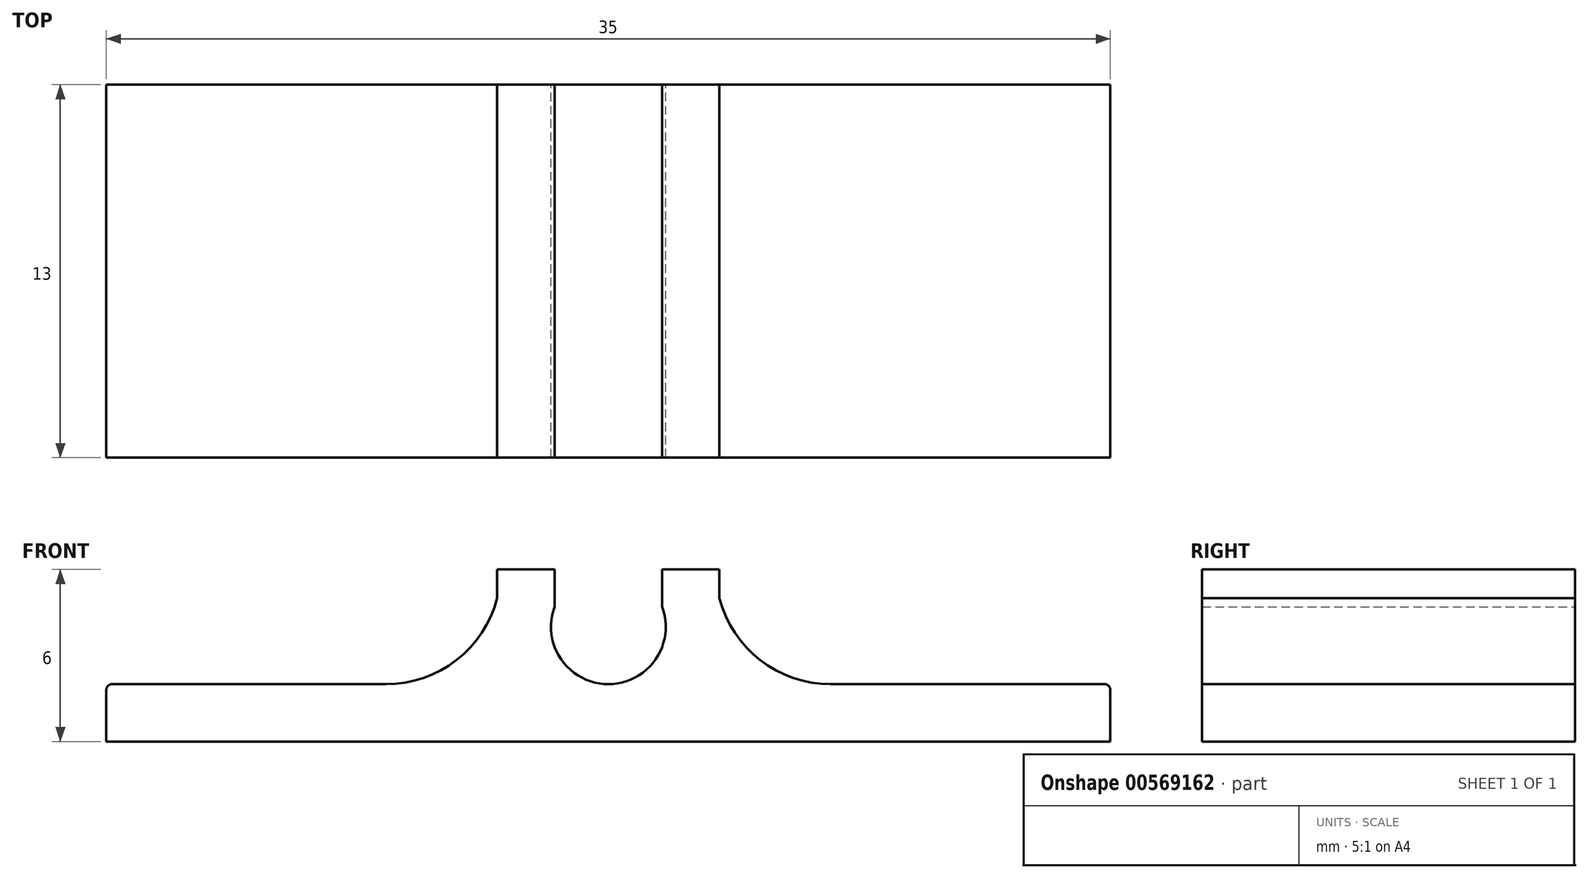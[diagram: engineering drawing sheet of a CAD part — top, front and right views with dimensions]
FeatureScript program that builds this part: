
annotation { "Feature Type Name" : "Feature", "Feature Type Description" : "" }
export const myFeature = defineFeature(function(context is Context, id is Id, definition is map)
    precondition{}
    {
        {
            var Q0;
            Q0=qCreatedBy(makeId("Front.planeOp"),FACE);
            var sketch = newSketch(context, id + "F0", { "sketchPlane" : qUnion([Q0])});
            skLineSegment(sketch, "E0.bottom", {"start": v(-17.5, 1) * mm, "end": v(17.5, 1) * mm});
            skLineSegment(sketch, "E0.top", {"start": v(-17.5, -1) * mm, "end": v(17.5, -1) * mm});
            skLineSegment(sketch, "E0.left", {"start": v(-17.5, 1) * mm, "end": v(-17.5, -1) * mm});
            skLineSegment(sketch, "E0.right", {"start": v(17.5, 1) * mm, "end": v(17.5, -1) * mm});
            skLineSegment(sketch, "E1", {"start": v(0, 1) * mm, "end": v(0, -1) * mm, "construction": true});
            skLineSegment(sketch, "E2", {"start": v(17.5, 0) * mm, "end": v(-17.5, 0) * mm, "construction": true});
            skLineSegment(sketch, "E3", {"start": v(-6.74, 3.7) * mm, "end": v(5.44, 3.7) * mm});
            skArc(sketch, "E4", {"start": v(1.87, 3.7) * mm, "mid": v(0, 5) * mm, "end": v(-1.87, 3.7) * mm, "construction": true});
            skArc(sketch, "E5", {"start": v(-1.87, 3.7) * mm, "mid": v(0, 1) * mm, "end": v(1.87, 3.7) * mm});
            skArc(sketch, "E6.0", {"start": v(-3.87, 4) * mm, "mid": v(0, -1) * mm, "end": v(3.87, 4) * mm});
            skLineSegment(sketch, "E7", {"start": v(-1.87, 3.7) * mm, "end": v(-1.87, 5) * mm});
            skLineSegment(sketch, "E8", {"start": v(-1.87, 5) * mm, "end": v(-3.87, 5) * mm});
            skLineSegment(sketch, "E9", {"start": v(-3.87, 5) * mm, "end": v(-3.87, 4) * mm});
            skLineSegment(sketch, "E10.MirrorCS", {"start": v(1.87, 3.7) * mm, "end": v(1.87, 5) * mm});
            skLineSegment(sketch, "E11.MirrorCS", {"start": v(1.87, 5) * mm, "end": v(3.87, 5) * mm});
            skLineSegment(sketch, "E12.MirrorCS", {"start": v(3.87, 5) * mm, "end": v(3.87, 4) * mm});
            skSolve(sketch);
        }
        {
            var Q0;
            {var subQ4=sQuery(id+"F0.wireOp",EDGE,"b06215e1-c406-422c-8c48-e48db1ec31c51");Q0=makeQuery(id+"F0.imprint","IMPRINT",FACE,{"disambiguationData":[TD([[makeQuery(id+"F0.imprint","IMPRINT",EDGE,{"derivedFrom":subQ4}),-1.0]])]});}
            var Q1;
            {var subQ4=sQuery(id+"F0.wireOp",EDGE,"f0d49411-302d-4f87-b0ff-6c94c2d25f7d0.MirrorCS");Q1=makeQuery(id+"F0.imprint","IMPRINT",FACE,{"disambiguationData":[TD([[makeQuery(id+"F0.imprint","IMPRINT",EDGE,{"derivedFrom":subQ4}),1.0]])]});}
            var Q2;
            Q2=makeQuery(id+"F0.imprint","IMPRINT",FACE,{"disambiguationData":[TD([[makeQuery(id+"F0.imprint","IMPRINT",EDGE,{"derivedFrom":sQuery(id+"F0.wireOp",EDGE,"E0.top")}),1.0]])]});
            var Q3;
            {var subQ0=sQuery(id+"F0.wireOp",EDGE,"On8rnizX-Pa3G-44f2-iiiQ-2S0TwAKPRwIm");Q3=makeQuery(id+"F0.imprint","IMPRINT",FACE,{"disambiguationData":[TD([[makeQuery(id+"F0.imprint","IMPRINT",EDGE,{"derivedFrom":subQ0}),-1.0]])]});}
            var Q4;
            {var subQ0=sQuery(id+"F0.wireOp",EDGE,"11dc987d-64fd-45dd-b81f-999d6c03d7ff2");var subQ1=sQuery(id+"F0.wireOp",EDGE,"E0.bottom");var subQ2=makeQuery(id+"F0.imprint","INTERSECT",VERTEX,{"disambiguationData":[OD(0.0)],"derivedFrom":[subQ1,subQ0]});Q4=makeQuery(id+"F0.imprint","IMPRINT",FACE,{"disambiguationData":[TD([[makeQuery(id+"F0.imprint","IMPRINT",EDGE,{"disambiguationData":[TD([[subQ2,-1.0]])],"derivedFrom":subQ1}),-1.0]])]});}
            var Q5;
            {var subQ0=sQuery(id+"F0.wireOp",EDGE,"11dc987d-64fd-45dd-b81f-999d6c03d7ff2");var subQ8=sQuery(id+"F0.wireOp",EDGE,"E0.bottom");var subQ9=makeQuery(id+"F0.imprint","INTERSECT",VERTEX,{"disambiguationData":[OD(0.0)],"derivedFrom":[subQ8,subQ0]});Q5=makeQuery(id+"F0.imprint","IMPRINT",FACE,{"disambiguationData":[TD([[makeQuery(id+"F0.imprint","IMPRINT",EDGE,{"disambiguationData":[TD([[subQ9,-1.0]])],"derivedFrom":subQ8}),1.0]])]});}
            var Q6;
            {var subQ3=sQuery(id+"F0.wireOp",EDGE,"E0.bottom");var subQ5=sQuery(id+"F0.wireOp",EDGE,"b06215e1-c406-422c-8c48-e48db1ec31c51");var subQ10=makeQuery(id+"F0.imprint","INTERSECT",VERTEX,{"disambiguationData":[OD(1.0)],"derivedFrom":[subQ3,subQ5]});Q6=makeQuery(id+"F0.imprint","IMPRINT",FACE,{"disambiguationData":[TD([[makeQuery(id+"F0.imprint","IMPRINT",EDGE,{"disambiguationData":[TD([[subQ10,-1.0]])],"derivedFrom":subQ3}),1.0]])]});}
            var Q7;
            {var subQ0=sQuery(id+"F0.wireOp",EDGE,"11dc987d-64fd-45dd-b81f-999d6c03d7ff2");var subQ1=sQuery(id+"F0.wireOp",EDGE,"f0d49411-302d-4f87-b0ff-6c94c2d25f7d0.MirrorCS");var subQ2=makeQuery(id+"F0.imprint","INTERSECT",VERTEX,{"disambiguationData":[OD(0.0)],"derivedFrom":[subQ1,subQ0]});Q7=makeQuery(id+"F0.imprint","IMPRINT",FACE,{"disambiguationData":[TD([[makeQuery(id+"F0.imprint","IMPRINT",EDGE,{"disambiguationData":[TD([[subQ2,-1.0]])],"derivedFrom":subQ1}),-1.0]])]});}
            var Q8;
            {var subQ0=sQuery(id+"F0.wireOp",EDGE,"11dc987d-64fd-45dd-b81f-999d6c03d7ff2");var subQ1=sQuery(id+"F0.wireOp",EDGE,"On8rnizX-Pa3G-44f2-iiiQ-2S0TwAKPRwIm");var subQ2=makeQuery(id+"F0.imprint","INTERSECT",VERTEX,{"disambiguationData":[OD(0.0)],"derivedFrom":[subQ1,subQ0]});Q8=makeQuery(id+"F0.imprint","IMPRINT",FACE,{"disambiguationData":[TD([[makeQuery(id+"F0.imprint","IMPRINT",EDGE,{"disambiguationData":[TD([[subQ2,-1.0]])],"derivedFrom":subQ1}),1.0]])]});}
            var Q9;
            {var subQ0=sQuery(id+"F0.wireOp",EDGE,"E6.0");var subQ1=sQuery(id+"F0.wireOp",EDGE,"E0.bottom");var subQ2=makeQuery(id+"F0.imprint","INTERSECT",VERTEX,{"disambiguationData":[OD(1.0)],"derivedFrom":[subQ1,subQ0]});Q9=makeQuery(id+"F0.imprint","IMPRINT",FACE,{"disambiguationData":[TD([[makeQuery(id+"F0.imprint","IMPRINT",EDGE,{"disambiguationData":[TD([[subQ2,1.0]])],"derivedFrom":subQ1}),1.0]])]});}
            var Q10;
            {var subQ0=sQuery(id+"F0.wireOp",EDGE,"E7");Q10=makeQuery(id+"F0.imprint","IMPRINT",FACE,{"disambiguationData":[TD([[makeQuery(id+"F0.imprint","IMPRINT",EDGE,{"derivedFrom":subQ0}),1.0]])]});}
            var Q11;
            {var subQ0=sQuery(id+"F0.wireOp",EDGE,"E10.MirrorCS");Q11=makeQuery(id+"F0.imprint","IMPRINT",FACE,{"disambiguationData":[TD([[makeQuery(id+"F0.imprint","IMPRINT",EDGE,{"derivedFrom":subQ0}),-1.0]])]});}
            extrude(context, id + "F1", {"entities" : qUnion([Q0, Q1, Q2, Q3, Q4, Q5, Q6, Q7, Q8, Q9, Q10, Q11]), "depth" : 13 * mm, "offsetDistance" : 25 * mm});
        }
        {
            var Q0;
            {var subQ0=sQuery(id+"F0.wireOp",EDGE,"11dc987d-64fd-45dd-b81f-999d6c03d7ff2");var subQ1=sQuery(id+"F0.wireOp",EDGE,"E0.bottom");Q0=makeQuery(id+"F1.opExtrude","SWEPT_EDGE",EDGE,{"disambiguationData":[OSD([subQ1,subQ0]),TDD([makeQuery(id+"F0.imprint","INTERSECT",VERTEX,{"disambiguationData":[OD(0.0)],"derivedFrom":[subQ1,subQ0]})])]});}
            var Q1;
            {var subQ0=sQuery(id+"F0.wireOp",EDGE,"11dc987d-64fd-45dd-b81f-999d6c03d7ff2");var subQ1=sQuery(id+"F0.wireOp",EDGE,"E0.bottom");Q1=makeQuery(id+"F1.opExtrude","SWEPT_EDGE",EDGE,{"disambiguationData":[OSD([subQ1,subQ0]),TDD([makeQuery(id+"F0.imprint","INTERSECT",VERTEX,{"disambiguationData":[OD(1.0)],"derivedFrom":[subQ1,subQ0]})])]});}
            fillet(context, id + "F2", {"entities" : qUnion([Q0, Q1]), "radius" : 4 * mm, "tangentPropagation" : true, "allowEdgeOverflow" : false});
        }
        {
            var Q0;
            Q0=makeQuery(id+"F1.opExtrude","SWEPT_EDGE",EDGE,{"disambiguationData":[OSD([sQuery(id+"F0.wireOp",EDGE,"9d8f70ee-38eb-47e2-91bf-544f87467fa90.MirrorCS"),sQuery(id+"F0.wireOp",EDGE,"2089c7ef-90f4-481e-98d7-70f38c17ba5b0.MirrorCS")])]});
            var Q1;
            Q1=makeQuery(id+"F1.opExtrude","SWEPT_EDGE",EDGE,{"disambiguationData":[OSD([sQuery(id+"F0.wireOp",EDGE,"f0d49411-302d-4f87-b0ff-6c94c2d25f7d0.MirrorCS"),sQuery(id+"F0.wireOp",EDGE,"2089c7ef-90f4-481e-98d7-70f38c17ba5b0.MirrorCS")])]});
            var Q2;
            Q2=makeQuery(id+"F1.opExtrude","SWEPT_EDGE",EDGE,{"disambiguationData":[OSD([sQuery(id+"F0.wireOp",EDGE,"3463b64b-17f2-4f9b-800d-9c95dd4d804c.0"),sQuery(id+"F0.wireOp",EDGE,"gHcYY1jY-9el1-v0DO-zF6A-s3sRlDlnzs8D")])]});
            var Q3;
            Q3=makeQuery(id+"F1.opExtrude","SWEPT_EDGE",EDGE,{"disambiguationData":[OSD([sQuery(id+"F0.wireOp",EDGE,"On8rnizX-Pa3G-44f2-iiiQ-2S0TwAKPRwIm"),sQuery(id+"F0.wireOp",EDGE,"gHcYY1jY-9el1-v0DO-zF6A-s3sRlDlnzs8D")])]});
            var Q4;
            Q4=makeQuery(id+"F1.opExtrude","SWEPT_EDGE",EDGE,{"disambiguationData":[OSD([sQuery(id+"F0.wireOp",EDGE,"E0.bottom"),sQuery(id+"F0.wireOp",EDGE,"E0.left")])]});
            var Q5;
            Q5=makeQuery(id+"F1.opExtrude","SWEPT_EDGE",EDGE,{"disambiguationData":[OSD([sQuery(id+"F0.wireOp",EDGE,"E0.bottom"),sQuery(id+"F0.wireOp",EDGE,"E0.right")])]});
            fillet(context, id + "F3", {"entities" : qUnion([Q0, Q1, Q2, Q3, Q4, Q5]), "radius" : 0.2 * mm, "tangentPropagation" : true, "allowEdgeOverflow" : false});
        }
    });
